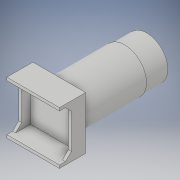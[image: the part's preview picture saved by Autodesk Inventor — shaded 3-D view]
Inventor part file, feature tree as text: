
AUTODESK INVENTOR PART (.ipt)
format: ipt  version: 2018 (Build 220112000, 112)  size: 148,992 bytes
history: native  units: in
note: dims shown in document units (in); Inventor stores cm internally (conversion verified against a paired STEP export)
features: extrude x5, sketch x5, chamfer x1
ambient origin geometry x8: Origin, YZ Plane, XZ Plane, XY Plane, X Axis, Y Axis, Z Axis, Center Point
bodies: Solid1 (feature_tree)
feature tree (11):
  extrude  "Extrusion1"  Depth=0.6988in
  extrude  "Extrusion2"  Depth=0.3465in
  extrude  "Extrusion3"  Depth=0.8661in
  extrude  "Extrusion5"  Depth=0.0394in
  extrude  "Extrusion6"  Depth=0.2756in TaperAngle=0.0deg
  chamfer  "Chamfer1"  Distance=0.1575in
  sketch  "Sketch1"  dims[d0=0.6988in d1=0.6988in]
  sketch  "Sketch2"  dims[d2=0.3465in d3=0.0in d4=0.5807in]
  sketch  "Sketch3"  dims[d5=0.8661in d6=0.0in d7=0.5556in]
  sketch  "Sketch5"  dims[d8=0.2953in d9=0.0in d14=0.0394in]
  sketch  "Sketch6"  dims[d15=0.0394in d16=0.2756in d17=0.0in d18=0.1575in d19=0.0in d20=0.0787in d21=0.125in d22=45.0deg]
